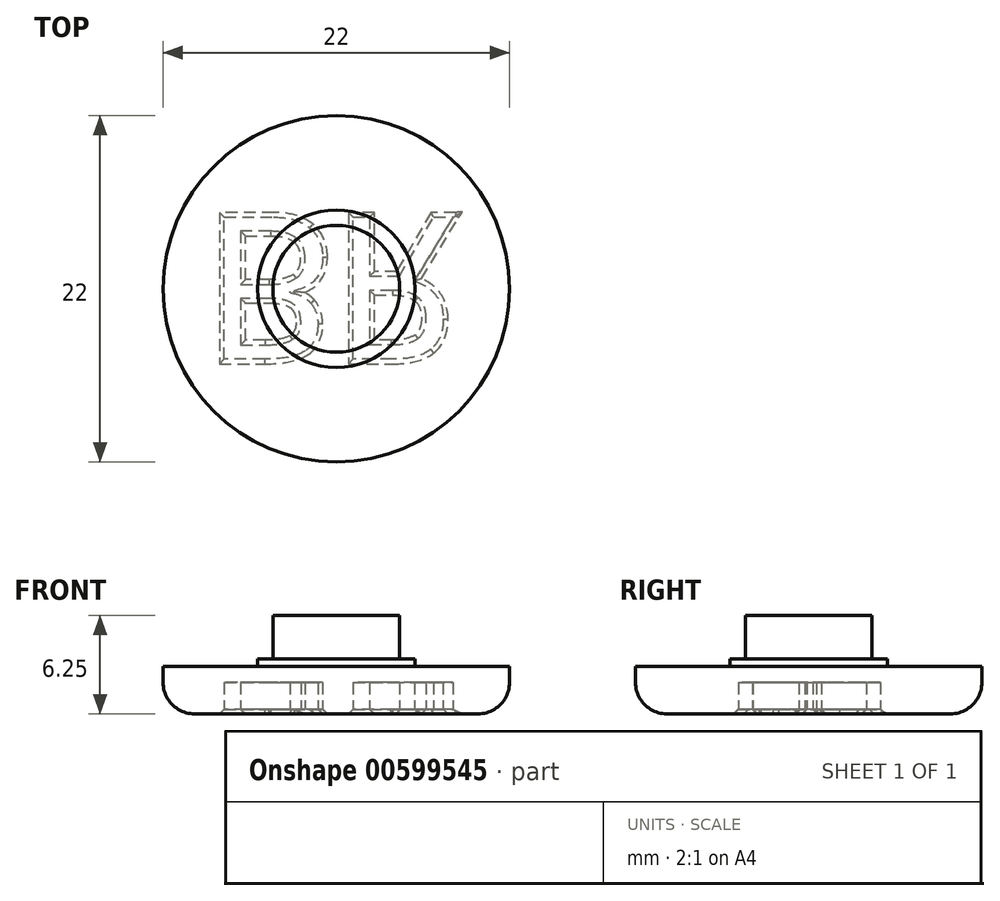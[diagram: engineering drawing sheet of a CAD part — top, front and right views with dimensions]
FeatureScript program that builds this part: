
annotation { "Feature Type Name" : "Feature", "Feature Type Description" : "" }
export const myFeature = defineFeature(function(context is Context, id is Id, definition is map)
    precondition{}
    {
        {
            var Q0;
            Q0=qCreatedBy(makeId("Top.planeOp"),FACE);
            var sketch = newSketch(context, id + "F0", { "sketchPlane" : qUnion([Q0])});
            skCircle(sketch, "E0", {"center": v(0, 0) * mm, "radius": 11 * mm});
            skSolve(sketch);
        }
        {
            var Q0;
            Q0 = qSketchRegion(id + "F0", true);
            extrude(context, id + "F1", {"entities" : qUnion([Q0]), "depth" : 3 * mm, "offsetDistance" : 25 * mm});
        }
        {
            var Q0;
            Q0=makeQuery(id+"F1.opExtrude","CAP_EDGE",EDGE,{"disambiguationData":[OSD([sQuery(id+"F0.wireOp",EDGE,"E0")])],"isStart":true});
            fillet(context, id + "F2", {"entities" : qUnion([Q0]), "radius" : 2 * mm, "tangentPropagation" : true, "allowEdgeOverflow" : false});
        }
        {
            var Q0;
            Q0=makeQuery(id+"F1.opExtrude","CAP_FACE",FACE,{"disambiguationData":[OSD([sQuery(id+"F0.wireOp",EDGE,"E0")])],"isStart":false});
            var sketch = newSketch(context, id + "F3", { "sketchPlane" : qUnion([Q0])});
            skCircle(sketch, "E1", {"center": v(0, 0) * mm, "radius": 5 * mm});
            skCircle(sketch, "E2", {"center": v(0, 0) * mm, "radius": 4.03 * mm});
            skSolve(sketch);
        }
        {
            var Q0;
            Q0=makeQuery(id+"F3.imprint","IMPRINT",FACE,{"disambiguationData":[TD([[makeQuery(id+"F3.imprint","IMPRINT",EDGE,{"derivedFrom":sQuery(id+"F3.wireOp",EDGE,"E1")}),1.0]])]});
            extrude(context, id + "F4", {"entities" : qUnion([Q0]), "operationType" : NewBodyOperationType.ADD, "depth" : 0.5 * mm, "offsetDistance" : 25 * mm});
        }
        {
            var Q0;
            Q0=makeQuery(id+"F4.boolean.opBoolean","SPLIT",FACE,{"disambiguationData":[TD([makeQuery(id+"F4.opExtrude","SWEPT_FACE",FACE,{"disambiguationData":[OSD([sQuery(id+"F3.wireOp",EDGE,"E2")])]})])],"derivedFrom":makeQuery(id+"F1.opExtrude","CAP_FACE",FACE,{"disambiguationData":[OSD([sQuery(id+"F0.wireOp",EDGE,"E0")])],"isStart":false})});
            extrude(context, id + "F5", {"entities" : qUnion([Q0]), "operationType" : NewBodyOperationType.ADD, "depth" : 3.25 * mm, "offsetDistance" : 25 * mm});
        }
        {
            var Q0;
            Q0=makeQuery(id+"F1.opExtrude","CAP_FACE",FACE,{"disambiguationData":[OSD([sQuery(id+"F0.wireOp",EDGE,"E0")])],"isStart":true});
            var sketch = newSketch(context, id + "F6", { "sketchPlane" : qUnion([Q0])});
            skText(sketch, "E3", { "text": "BR\n", "fontName": "OpenSans-Regular.ttf"});
            const initialGuessF6  = {"E3": [-0.00836, -0.00455, 1, 0, 0.0091]};
            skSetInitialGuess(sketch, initialGuessF6);
            skSolve(sketch);
        }
        {
            var Q0;
            Q0 = qSketchRegion(id + "F6", true);
            var Q1;
            Q1 = qConstructionFilter(qBodyType(qCreatedBy(id + "F6" ,EDGE), BodyType.WIRE), ConstructionObject.NO);
            extrude(context, id + "F7", {"entities" : qUnion([Q0]), "operationType" : NewBodyOperationType.REMOVE, "surfaceEntities" : qUnion([Q1]), "oppositeDirection" : true, "depth" : 2 * mm, "offsetDistance" : 25 * mm});
        }
        {
            var Q0;
            Q0=makeQuery(id+"F1.opExtrude","CAP_FACE",FACE,{"disambiguationData":[OSD([sQuery(id+"F0.wireOp",EDGE,"E0")])],"isStart":true});
            chamfer(context, id + "F8", {"entities" : qUnion([Q0]), "width" : 0.3 * mm, "tangentPropagation" : true});
        }
    });
